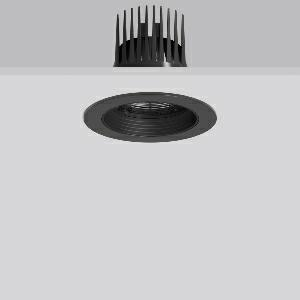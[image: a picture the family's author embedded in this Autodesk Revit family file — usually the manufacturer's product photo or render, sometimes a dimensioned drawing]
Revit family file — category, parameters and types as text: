
# Revit family: heledon_maxi_e_901783_003_e9ac
name_source: partatom
category: Lighting Fixtures
units: mm (PartAtom-declared; Revit-internal decimal feet)

## family parameters
Cut with Voids When Loaded = No
Host = Face
Light Source = No
Part Type = Normal
Room Calculation Point = No
Round Connector Dimension = Use Diameter
Shared = No

## types (1)
- HELEDON maxi E (1 x LED Modul 920 meat+, 1900 lm, 2000)
    Apparent Load = 33 VA
    Approval mark = CE
    CIE Flux Codes = 96 99 100 100 100
    Color Rendering = 90
    Color Temperature = 2000
    Default Elevation = 1800 mm
    Description = Series: HELEDON maxi
Round recessed downlight. Housing: die-cast aluminium, powder-coated. Black plastic ring and recessed LED to prevent glare from the side. Optical assembly with lens made of plastic (polycarbonate) for the best homogeneous light distribution - can be changed without tools. Special LED for illumination of meat included. Suitable for Recessed ceiling mounting. Installation without tools thanks to spring fastening system. Including separate LED converter with connecting cable 600 mm.High quality converter without flickering and stroboscopic effect. Through-wiring box (5 pole) available as accessory. The following accessories can be mounted without use of tools: interchangeable lenses, decorative glasses, honeycomb louvre, clear and frosted diffusers, white interchangeable plastic ring. 
Colour: deep black, matt (RAL 9005)
Diameter: 162 mm
Height: 3 mm
Cut-out diameter: 152 mm
Recess height: 200 mm
Luminaire: recess height: 135 mm
Lamp: LED
Socket: without socket
Colour temperature: meat +
System power: 33 W
Rated luminous flux: 1900 lm
Luminous efficiency: 58 lm/W
Control gear: Regulated power supply
Protection class: II
Type of protection: IP 20
    Height = 0 mm  [stored 0 ft]
    Lamp = 1 x LED Modul 920 meat+
    Lamp Light Flux = 1900 lm
    Lamp count = 1
    Length = 162 mm
    Lifetime = 50000 h
    Luminous efficacy = 58 lm/W
    Manufacturer = RZB
    ModVariant = No
    Model = 901783.003
    Mounting Place = Ceiling
    Mounting Type = Recessed
    Number of Poles = 1
    OnlyDefault = Yes
    Power Factor = 1
    Product Name = HELEDON maxi E
    Product group = Recessed downlights
    ProductGroupID = 402
    Protection Class = Protection class II
    Protection Degree = IP 20
    RLX_Detail_Level = 1
    RLX_Emergency_Light_Flux = 0 lm
    RLX_Emergency_Type = 0
    RLX_Emergency_Type_DB = No
    RlxData = <blob elided: 120837 chars, md5=42d9d54b>
    Socket = socket
    Standby Power = 0 W
    System Light Flux = 1900 lm
    System Power = 33 W
    Type Comments = Product without accessories
    Type Image = 901663.003.jpg
    URL = http://relux.com
    VarID = ---
    Voltage = 230 V
    Voltage Range = 220-240 V
    Weight = 0.00 kg
    Width = 0 mm  [stored 0 ft]

note: [stored X ft] marks values corroborated as IEEE doubles in the binary element streams (Revit-internal decimal feet)

## geometry (parser evidence)
native form markers: Blend x4, Sweep x12
no freeform markers — native parametric forms only
